# Revit family: Domotics-DomesticRanges-GEWISS-CHORUS_POWER-SOCKET-OUTLET_FRA
name_source: partatom
category: Apparecchi elettrici
revit_build: Autodesk Revit 2016 (Build: 20161004_0715(x64)
units: mm (PartAtom-declared; Revit-internal decimal feet)

## family parameters
Condiviso = Sì
Host = Superficie
Mantenere orientamento annotazione = Sì
Punto di calcolo locali = Sì
Quota connettore circolare = Usa diametro
Taglio con vuoti quando caricato = Sì
Tipo di parte = Normale

## types (10) — shared parameters
Breaking capacity: = 1.25 In (100 position changes)
Carico apparente = 0 VA
Catalogue = DOMOTICS
Catalogue Range = CHORUS - DOMESTIC RANGE
Category = Socket-outlet
Characteristics = With safety shields
Description. = Socket-outlet
Electrocod = 0131
For plug pins = Ã˜ 4 / 4.8 mm
Glow Wire Test = 850°C
IDF = ca032678-5032-499c-8887-160b7c004776
IDT = 8e79b32c-c3c2-4593-b20f-dce0ece3d5d6
Immagine tipo = GW14248.jpg
Insulation resistance = > 5 MOhm
N. poli = 1
No. Chorus modules = 2
No. Chorus modules: = 2
Produttore = GEWISS S.p.A.
Prolonged operation (no.of position changes) = 10.000 at In 250 V ac cosÃ˜=0,8
Prospetto di default = 1219 mm
Resistance at test voltage = 2000 V at 50 Hz for 1 minute
SEO = Socket outlet
Standard = French
Standard: = French
Standard; = IEC 60884-1; NF C 61-314
TXT ELETTRICO = 16
Technical sheet = https://www.gewiss.com
Terminal grip on cable traction = > 50 N
Terminal tightening capacity flexible cables (mm2) = min. 0,75 - max. 2x4
Terminal tightening capacity rigid cables (mm2) = min. 0,5 - max. 2x2,5
Thermo-pressure with ball = 125
Tipo_ = Chorus Prese Fra_GENERICO : GW14248 Presa 2M 2P+T 16A morsetti frontali standard Francese titanio
URL = https://www.gewiss.com
Version file RFA = 19.0
Volt = 230 V
Voltage = 250 V ac
Voltage: = 250 V ac

## per-type parameters (varying)
| type | Colour | Description: | Descrizione | EAN code | Modello | Type | Type: | Wiring terminals |
| GW14247 - Socket outlet 2M 2P+E 16A french st titanium | Titanium | 2P+E - 16A | SOCKET 2M 2P+E 16A FRENCH ST TITANIUM | 8011564266384 | GW14247 |  |  | With screw |
| GW12246 - Socket outlet 2M 2P 16A french st black | Black | 2P - 16A | SOCKET 2M 2P 16A FRENCH ST BLACK | 8011564266926 | GW12246 |  |  | With screw |
| GW14246 - Socket outlet 2M 2P 16A french st titanium | Titanium | 2P - 16A | SOCKET 2M 2P 16A FRENCH ST TITANIUM | 8011564266377 | GW14246 |  |  | With screw |
| GW14248 - Socket outlet 2M 2P+E 16A french o.fr.term.ti. | Titanium | 2P+E - 16A | 2M 2P+E 16A FRENCH SOCKET O.FR.TERM.TI. | 8011564292772 | GW14248 |  |  | Screws with front tightening terminals |
| GW12247 - Socket outlet 2M 2P+E 16A french st black | Black | 2P+E - 16A | SOCKET 2M 2P+E 16A FRENCH ST BLACK | 8011564266933 | GW12247 |  |  | With screw |
| GW10247 - Socket outlet outlet 2M 2P+E 16A fr st white | White | 2P+E - 16A | SOCKET OUTLET 2M 2P+E 16A FR ST WHITE | 8011564257979 | GW10247 |  |  | With screw |
| GW10258 - Socket outlet 2M 2P+E 16A fr front term. Red | Red | 2P+E - 16A | S. OUTL. 2M 2P+E 16A FR FRONT TERM. RED | 8011564292819 | GW10258 | For allocated lines | For allocated lines | Screws with front tightening terminals |
| GW12248 - Socket outlet 2M 2P+E 16A french o.fr.term.bl. | Black | 2P+E - 16A | 2M 2P+E 16A FRENCH SOCKET O.FR.TERM.BL. | 8011564292765 | GW12248 |  |  | Screws with front tightening terminals |
| GW10246 - Socket outlet outlet 2M 2P 16A fr st white | White | 2P - 16A | SOCKET OUTLET 2M 2P 16A FR ST WHITE | 8011564257962 | GW10246 |  |  | With screw |
| GW10248 - Socket outlet2M 2P+E 16A fr front term. Wh | White | 2P+E - 16A | S. OUTL. 2M 2P+E 16A FR FRONT TERM. WH | 8011564292758 | GW10248 |  |  | Screws with front tightening terminals |

note: source unit labels omitted for Thermo-pressure with ball — the stored unit's dimension contradicts the parameter name (converter mislabeling)

## geometry (parser evidence)
native form markers: Sweep x2
no freeform markers — native parametric forms only
